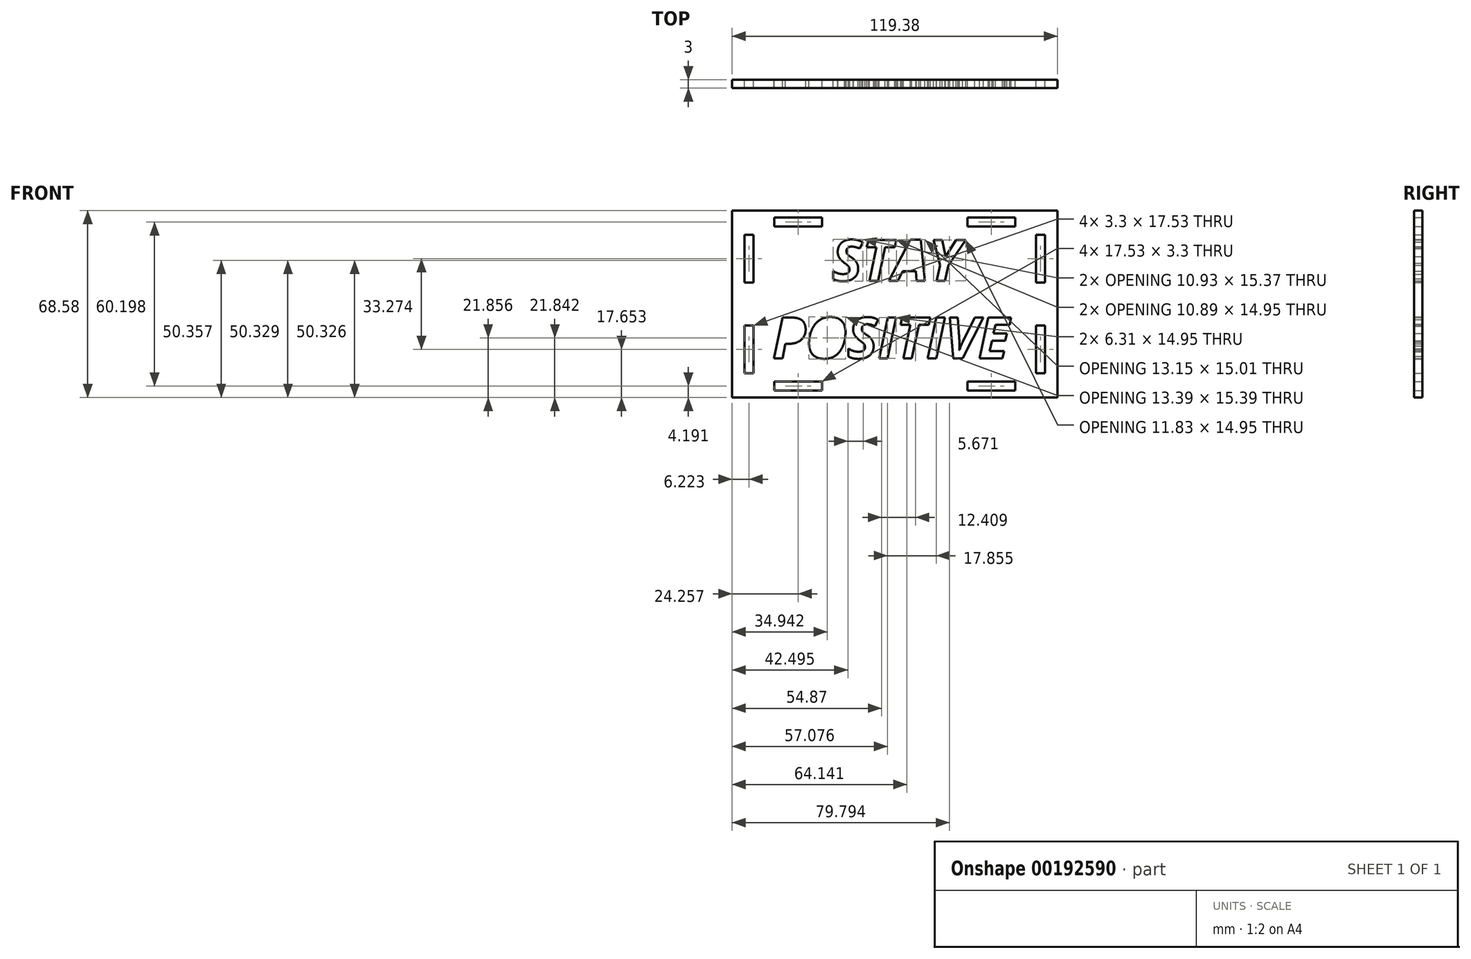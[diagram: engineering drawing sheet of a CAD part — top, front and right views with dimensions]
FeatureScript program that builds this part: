
annotation { "Feature Type Name" : "Feature", "Feature Type Description" : "" }
export const myFeature = defineFeature(function(context is Context, id is Id, definition is map)
    precondition{}
    {
        {
            var Q0;
            Q0=qCreatedBy(makeId("Front.planeOp"),FACE);
            var sketch = newSketch(context, id + "F0", { "sketchPlane" : qUnion([Q0])});
            skLineSegment(sketch, "E0.bottom", {"start": v(59.7, -34.3) * mm, "end": v(-59.7, -34.3) * mm});
            skLineSegment(sketch, "E0.top", {"start": v(59.7, 34.3) * mm, "end": v(-59.7, 34.3) * mm});
            skLineSegment(sketch, "E0.left", {"start": v(59.7, -34.3) * mm, "end": v(59.7, 34.3) * mm});
            skLineSegment(sketch, "E0.right", {"start": v(-59.7, -34.3) * mm, "end": v(-59.7, 34.3) * mm});
            skPoint(sketch, "E0.middle", {"position": v(0, 0) * mm});
            skText(sketch, "E1", { "text": "    STAY\nPOSITIVE", "fontName": "OpenSans-BoldItalic.ttf"});
            skLineSegment(sketch, "E2.bottom", {"start": v(-55.12, 25.4) * mm, "end": v(-51.82, 25.4) * mm});
            skLineSegment(sketch, "E3", {"start": v(-55.12, 25.4) * mm, "end": v(-55.12, 7.87) * mm});
            skLineSegment(sketch, "E4", {"start": v(-55.12, 7.87) * mm, "end": v(-51.82, 7.87) * mm});
            skLineSegment(sketch, "E5", {"start": v(-51.82, 7.87) * mm, "end": v(-51.82, 25.4) * mm});
            skLineSegment(sketch, "E6.MirrorCS", {"start": v(-55.12, -25.4) * mm, "end": v(-55.12, -7.87) * mm});
            skLineSegment(sketch, "E7.MirrorCS", {"start": v(-51.82, -7.87) * mm, "end": v(-51.82, -25.4) * mm});
            skLineSegment(sketch, "E8.MirrorCS", {"start": v(-55.12, -25.4) * mm, "end": v(-51.82, -25.4) * mm});
            skLineSegment(sketch, "E9.MirrorCS", {"start": v(-55.12, -7.87) * mm, "end": v(-51.82, -7.87) * mm});
            skLineSegment(sketch, "E10.MirrorCS", {"start": v(51.82, 7.87) * mm, "end": v(51.82, 25.4) * mm});
            skLineSegment(sketch, "E11.MirrorCS", {"start": v(55.12, 25.4) * mm, "end": v(55.12, 7.87) * mm});
            skLineSegment(sketch, "E12.MirrorCS", {"start": v(55.12, 7.87) * mm, "end": v(51.82, 7.87) * mm});
            skLineSegment(sketch, "E13.MirrorCS", {"start": v(55.12, 25.4) * mm, "end": v(51.82, 25.4) * mm});
            skLineSegment(sketch, "E14.MirrorCS", {"start": v(55.12, -25.4) * mm, "end": v(51.82, -25.4) * mm});
            skLineSegment(sketch, "E15.MirrorCS", {"start": v(55.12, -25.4) * mm, "end": v(55.12, -7.87) * mm});
            skLineSegment(sketch, "E16.MirrorCS", {"start": v(51.82, -7.87) * mm, "end": v(51.82, -25.4) * mm});
            skLineSegment(sketch, "E17.MirrorCS", {"start": v(55.12, -7.87) * mm, "end": v(51.82, -7.87) * mm});
            skLineSegment(sketch, "E18", {"start": v(-44.2, -28.45) * mm, "end": v(-26.67, -28.45) * mm});
            skLineSegment(sketch, "E19", {"start": v(-26.67, -28.45) * mm, "end": v(-26.67, -31.75) * mm});
            skLineSegment(sketch, "E20", {"start": v(-26.67, -31.75) * mm, "end": v(-44.2, -31.75) * mm});
            skLineSegment(sketch, "E21", {"start": v(-44.2, -31.75) * mm, "end": v(-44.2, -28.45) * mm});
            skLineSegment(sketch, "E22.MirrorCS", {"start": v(-44.2, 28.45) * mm, "end": v(-26.67, 28.45) * mm});
            skLineSegment(sketch, "E23.MirrorCS", {"start": v(-26.67, 31.75) * mm, "end": v(-44.2, 31.75) * mm});
            skLineSegment(sketch, "E24.MirrorCS", {"start": v(-26.67, 28.45) * mm, "end": v(-26.67, 31.75) * mm});
            skLineSegment(sketch, "E25.MirrorCS", {"start": v(-44.2, 31.75) * mm, "end": v(-44.2, 28.45) * mm});
            skLineSegment(sketch, "E26.MirrorCS", {"start": v(26.67, -28.45) * mm, "end": v(26.67, -31.75) * mm});
            skLineSegment(sketch, "E27.MirrorCS", {"start": v(44.2, -28.45) * mm, "end": v(26.67, -28.45) * mm});
            skLineSegment(sketch, "E28.MirrorCS", {"start": v(44.2, -31.75) * mm, "end": v(44.2, -28.45) * mm});
            skLineSegment(sketch, "E29.MirrorCS", {"start": v(26.67, -31.75) * mm, "end": v(44.2, -31.75) * mm});
            skLineSegment(sketch, "E30.MirrorCS", {"start": v(44.2, 28.45) * mm, "end": v(26.67, 28.45) * mm});
            skLineSegment(sketch, "E31.MirrorCS", {"start": v(26.67, 31.75) * mm, "end": v(44.2, 31.75) * mm});
            skLineSegment(sketch, "E32.MirrorCS", {"start": v(26.67, 28.45) * mm, "end": v(26.67, 31.75) * mm});
            skLineSegment(sketch, "E33.MirrorCS", {"start": v(44.2, 31.75) * mm, "end": v(44.2, 28.45) * mm});
            const initialGuessF0  = {"E1": [-0.04485, 0.00856, 1, 0, 0.01508]};
            skSetInitialGuess(sketch, initialGuessF0);
            skSolve(sketch);
        }
        {
            var Q0;
            Q0=makeQuery(id+"F0.imprint","IMPRINT",FACE,{"disambiguationData":[TD([[makeQuery(id+"F0.imprint","IMPRINT",EDGE,{"derivedFrom":sQuery(id+"F0.wireOp",EDGE,"E0.bottom")}),-1.0]])]});
            extrude(context, id + "F1", {"entities" : qUnion([Q0]), "depth" : 3 * mm});
        }
    });
